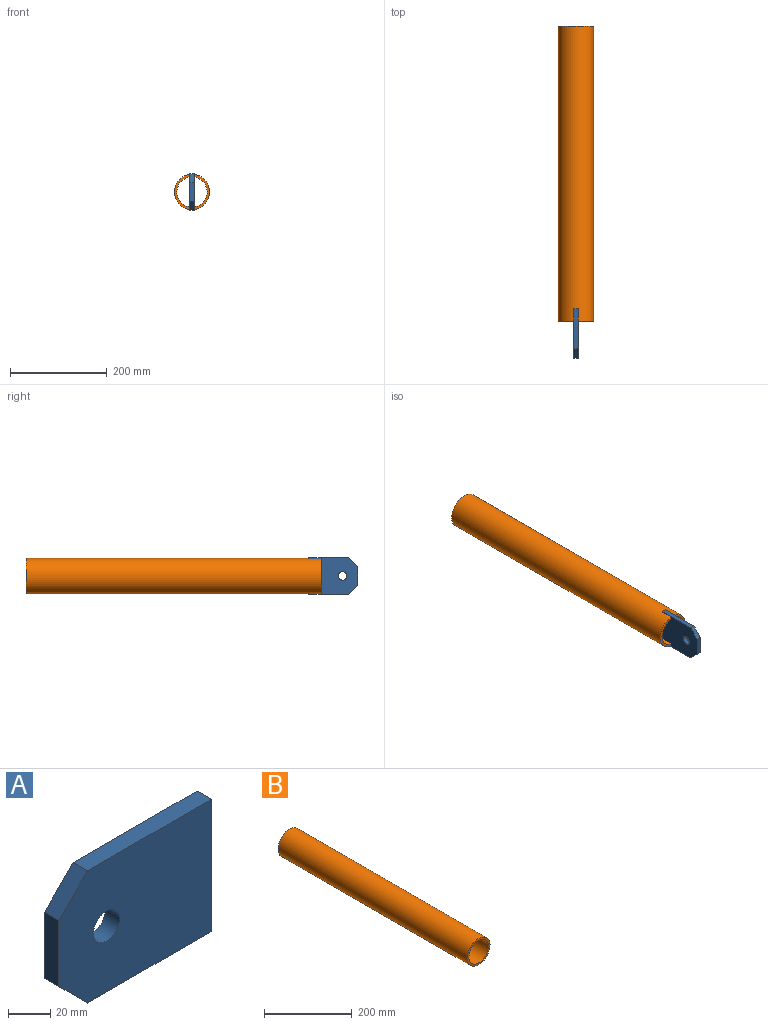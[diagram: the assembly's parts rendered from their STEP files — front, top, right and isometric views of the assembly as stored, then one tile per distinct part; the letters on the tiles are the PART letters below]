
ASSEMBLY  parts=2 mates=1
PART A: 9 faces, bbox 101.6x9.5x76.2 mm
  f0: plane 82.55x9.53mm, normal (0,0,1), area 786.3mm2, adj f1,f5,f7,f8
  f1: plane 19.05x19.05mm, normal (-0.71,0,0.71), area 256.6mm2, adj f0,f2,f7,f8
  f2: plane 38.1x9.53mm, normal (-1,0,0), area 362.9mm2, adj f1,f3,f7,f8
  f3: plane 19.05x19.05mm, normal (-0.71,0,-0.71), area 256.6mm2, adj f2,f4,f7,f8
  f4: plane 82.55x9.53mm, normal (0,0,-1), area 786.3mm2, adj f3,f5,f7,f8
  f5: plane 76.2x9.53mm, normal (1,0,0), area 725.8mm2, adj f0,f4,f7,f8
  f6: cylinder r=8.73mm len=17.46mm, axis (0,1,0), area 522.5mm2, adj f7,f8
  f7: plane 101.6x76.2mm, normal (0,-1,0), area 7139.5mm2, adj f0,f1,f2,f3,f4,f5,f6
  f8: plane 101.6x76.2mm, normal (0,1,0), area 7139.5mm2, adj f0,f1,f2,f3,f4,f5,f6
PART B: 4 faces, bbox 73x609.6x73 mm
  f0: cylinder r=31.36mm len=609.6mm, axis (0,1,0), area 120101.8mm2, adj f2,f3
  f1: cylinder r=36.51mm len=609.6mm, axis (0,1,0), area 139851.3mm2, adj f2,f3
  f2: plane 73.03x73.03mm, normal (0,-1,0), area 1099.4mm2, adj f0,f1
  f3: plane 73.03x73.03mm, normal (0,1,0), area 1099.4mm2, adj f0,f1
PLACE A rot(axis=(0,0,1),90deg) t=(10.19,-267.47,72.65)mm
PLACE B t=(10.19,81.78,72.65)mm
MATE fastened A.f5 <-> B.f0  axis (0,1,0) through (10.19,-197.62,72.65)mm
